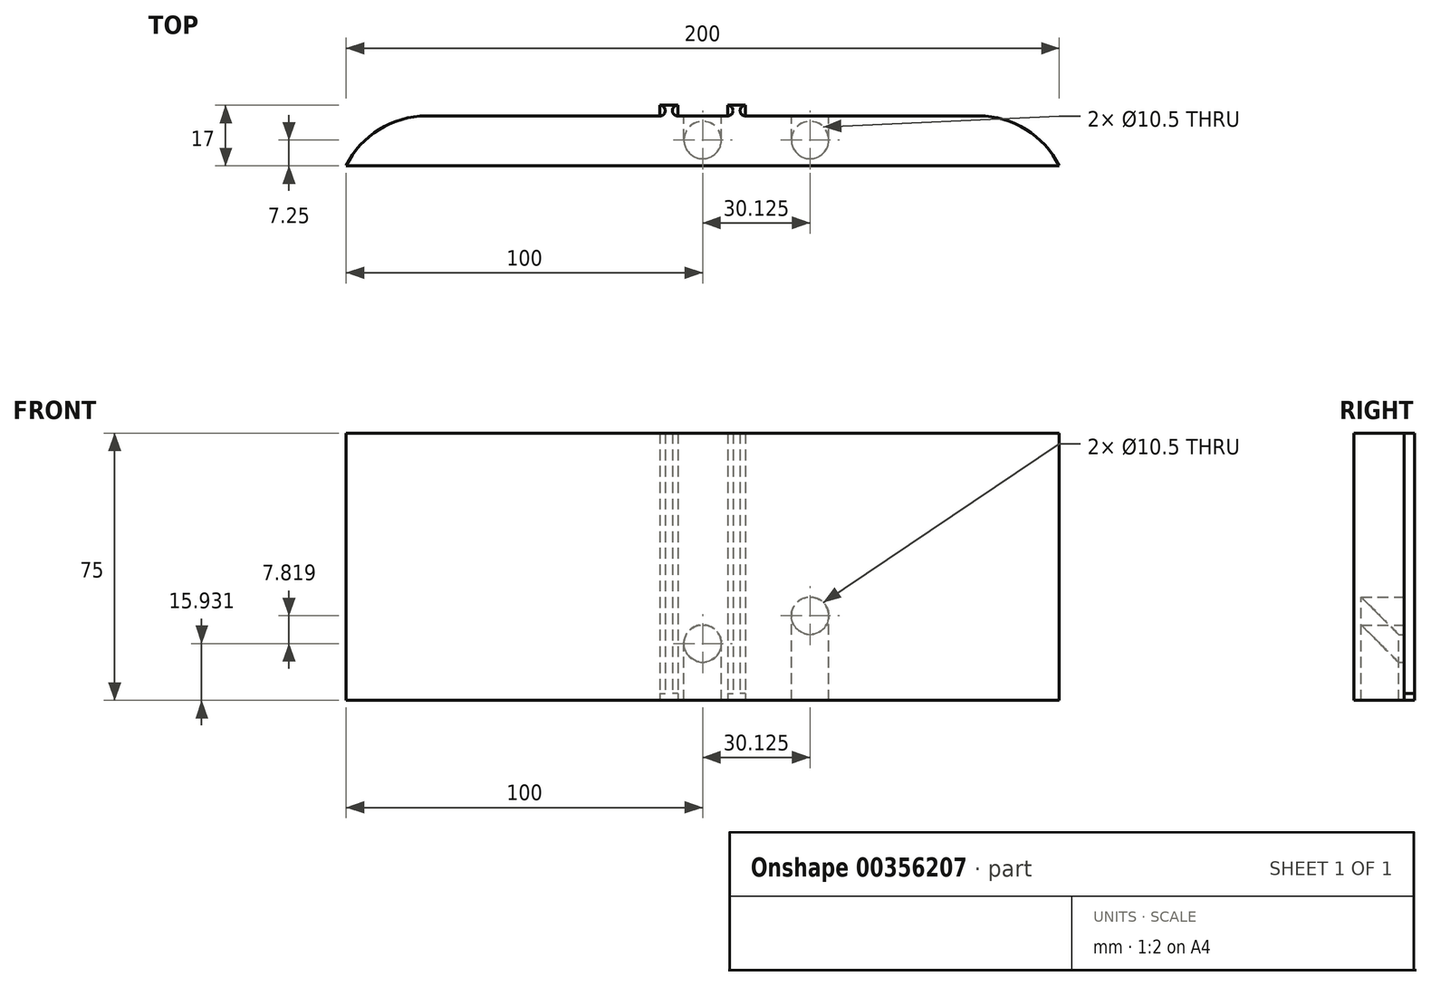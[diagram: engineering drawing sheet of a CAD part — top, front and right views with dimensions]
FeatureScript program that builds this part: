
annotation { "Feature Type Name" : "Feature", "Feature Type Description" : "" }
export const myFeature = defineFeature(function(context is Context, id is Id, definition is map)
    precondition{}
    {
        {
            var Q0;
            Q0=qCreatedBy(makeId("Top.planeOp"),FACE);
            var sketch = newSketch(context, id + "F0", { "sketchPlane" : qUnion([Q0])});
            skLineSegment(sketch, "E0.bottom", {"start": v(-13.85, 0) * mm, "end": v(12.1, 0) * mm});
            skLineSegment(sketch, "E0.top", {"start": v(-77.5, 14) * mm, "end": v(-12, 14) * mm});
            skArc(sketch, "E1", {"start": v(100, 0) * mm, "mid": v(90.75, 10.21) * mm, "end": v(77.5, 14) * mm});
            skArc(sketch, "E2", {"start": v(-77.5, 14) * mm, "mid": v(-90.75, 10.21) * mm, "end": v(-100, 0) * mm});
            skLineSegment(sketch, "E3", {"start": v(-100, 0) * mm, "end": v(-13.85, 0) * mm});
            skLineSegment(sketch, "E4", {"start": v(12.1, 0) * mm, "end": v(100, 0) * mm});
            skLineSegment(sketch, "E5.top", {"start": v(-12, 17) * mm, "end": v(-7, 17) * mm});
            skLineSegment(sketch, "E6.top", {"start": v(7, 17) * mm, "end": v(12, 17) * mm});
            skLineSegment(sketch, "E7.trimOffspring", {"start": v(-7, 14) * mm, "end": v(7, 14) * mm});
            skLineSegment(sketch, "E8.trimOffspring", {"start": v(12, 14) * mm, "end": v(77.5, 14) * mm});
            skCircle(sketch, "E9", {"center": v(30.13, 7.25) * mm, "radius": 5.25 * mm});
            skLineSegment(sketch, "E10.bottom", {"start": v(27, 14) * mm, "end": v(32.6, 14) * mm});
            skLineSegment(sketch, "E10.top", {"start": v(26.88, 11.37) * mm, "end": v(26.88, 11.37) * mm});
            skArc(sketch, "E11", {"start": v(-7, 17) * mm, "mid": v(-8.5, 15.5) * mm, "end": v(-7, 14) * mm});
            skArc(sketch, "E12", {"start": v(7, 14) * mm, "mid": v(8.5, 15.5) * mm, "end": v(7, 17) * mm});
            skArc(sketch, "E13", {"start": v(12, 17) * mm, "mid": v(10.5, 15.5) * mm, "end": v(12, 14) * mm});
            skPoint(sketch, "E14.start.orphan", {"position": v(-10.87, 14) * mm});
            skArc(sketch, "E15", {"start": v(-12, 14) * mm, "mid": v(-10.5, 15.5) * mm, "end": v(-12, 17) * mm});
            skPoint(sketch, "E10.right.end.orphan", {"position": v(33.38, 11.37) * mm});
            skLineSegment(sketch, "E16", {"start": v(7, 14) * mm, "end": v(7, 17) * mm});
            skLineSegment(sketch, "E17", {"start": v(12, 17) * mm, "end": v(12, 14) * mm});
            skLineSegment(sketch, "E18", {"start": v(-12, 14) * mm, "end": v(-12, 17) * mm});
            skLineSegment(sketch, "E19", {"start": v(-7, 17) * mm, "end": v(-7, 14) * mm});
            skLineSegment(sketch, "E20", {"start": v(-7, 14) * mm, "end": v(-12, 14) * mm});
            skLineSegment(sketch, "E21", {"start": v(12, 14) * mm, "end": v(7, 14) * mm});
            skCircle(sketch, "E22", {"center": v(0, 7.25) * mm, "radius": 5.25 * mm});
            skSolve(sketch);
        }
        {
            var Q0;
            Q0=makeQuery(id+"F0.imprint","IMPRINT",FACE,{"disambiguationData":[TD([[makeQuery(id+"F0.imprint","IMPRINT",EDGE,{"derivedFrom":sQuery(id+"F0.wireOp",EDGE,"E0.bottom")}),1.0]])]});
            var Q1;
            {var subQ0=sQuery(id+"F0.wireOp",EDGE,"E9");var subQ1=makeQuery(id+"F0.imprint","INTERSECT",VERTEX,{"derivedFrom":[subQ0,sQuery(id+"F0.wireOp",EDGE,"E10.left")]});Q1=makeQuery(id+"F0.imprint","IMPRINT",FACE,{"disambiguationData":[TD([[makeQuery(id+"F0.imprint","IMPRINT",EDGE,{"disambiguationData":[TD([[subQ1,1.0]])],"derivedFrom":subQ0}),1.0]])]});}
            var Q2;
            Q2=makeQuery(id+"F0.imprint","IMPRINT",FACE,{"disambiguationData":[TD([[makeQuery(id+"F0.imprint","IMPRINT",EDGE,{"derivedFrom":sQuery(id+"F0.wireOp",EDGE,"E10.bottom")}),-1.0]])]});
            var Q3;
            Q3=makeQuery(id+"F0.imprint","IMPRINT",FACE,{"disambiguationData":[TD([[makeQuery(id+"F0.imprint","IMPRINT",EDGE,{"derivedFrom":sQuery(id+"F0.wireOp",EDGE,"E9")}),1.0]])]});
            var Q4;
            Q4=makeQuery(id+"F0.imprint","IMPRINT",FACE,{"disambiguationData":[TD([[makeQuery(id+"F0.imprint","IMPRINT",EDGE,{"derivedFrom":sQuery(id+"F0.wireOp",EDGE,"E5.top")}),-1.0]])]});
            var Q5;
            Q5=makeQuery(id+"F0.imprint","IMPRINT",FACE,{"disambiguationData":[TD([[makeQuery(id+"F0.imprint","IMPRINT",EDGE,{"derivedFrom":sQuery(id+"F0.wireOp",EDGE,"E6.top")}),-1.0]])]});
            var Q6;
            Q6=makeQuery(id+"F0.imprint","IMPRINT",FACE,{"disambiguationData":[TD([[makeQuery(id+"F0.imprint","IMPRINT",EDGE,{"derivedFrom":sQuery(id+"F0.wireOp",EDGE,"E22")}),1.0]])]});
            extrude(context, id + "F1", {"entities" : qUnion([Q0, Q1, Q2, Q3, Q4, Q5, Q6]), "depth" : 75 * mm});
        }
        {
            var Q0;
            Q0=sQuery(id+"F0.wireOp",VERTEX,"E9.center");
            var Q1;
            Q1=qCreatedBy(makeId("Right.planeOp"),FACE);
            cPlane(context, id + "F2", {"entities" : qUnion([Q0, Q1]), "cplaneType" : CPlaneType.PLANE_POINT, "offset" : 25 * mm, "width" : 150 * mm, "height" : 150 * mm});
        }
        {
            var Q0;
            Q0=qCreatedBy(id+"F2.planeOp",FACE);
            var sketch = newSketch(context, id + "F3", { "sketchPlane" : qUnion([Q0])});
            skLineSegment(sketch, "E23", {"start": v(8, 0) * mm, "end": v(8, 23) * mm});
            skLineSegment(sketch, "E24", {"start": v(8, 23) * mm, "end": v(14, 23) * mm});
            skSolve(sketch);
        }
        {
            var Q0;
            Q0=makeQuery(id+"F0.imprint","IMPRINT",FACE,{"disambiguationData":[TD([[makeQuery(id+"F0.imprint","IMPRINT",EDGE,{"derivedFrom":sQuery(id+"F0.wireOp",EDGE,"E13")}),1.0]])]});
            var Q1;
            Q1=makeQuery(id+"F0.imprint","IMPRINT",FACE,{"disambiguationData":[TD([[makeQuery(id+"F0.imprint","IMPRINT",EDGE,{"derivedFrom":sQuery(id+"F0.wireOp",EDGE,"E12")}),1.0]])]});
            var Q2;
            Q2=makeQuery(id+"F0.imprint","IMPRINT",FACE,{"disambiguationData":[TD([[makeQuery(id+"F0.imprint","IMPRINT",EDGE,{"derivedFrom":sQuery(id+"F0.wireOp",EDGE,"E11")}),1.0]])]});
            var Q3;
            Q3=makeQuery(id+"F0.imprint","IMPRINT",FACE,{"disambiguationData":[TD([[makeQuery(id+"F0.imprint","IMPRINT",EDGE,{"derivedFrom":sQuery(id+"F0.wireOp",EDGE,"E15")}),1.0]])]});
            var Q4;
            Q4=makeQuery(id+"F0.imprint","IMPRINT",FACE,{"disambiguationData":[TD([[makeQuery(id+"F0.imprint","IMPRINT",EDGE,{"derivedFrom":sQuery(id+"F0.wireOp",EDGE,"E5.top")}),-1.0]])]});
            var Q5;
            Q5=makeQuery(id+"F0.imprint","IMPRINT",FACE,{"disambiguationData":[TD([[makeQuery(id+"F0.imprint","IMPRINT",EDGE,{"derivedFrom":sQuery(id+"F0.wireOp",EDGE,"E6.top")}),-1.0]])]});
            extrude(context, id + "F4", {"entities" : qUnion([Q0, Q1, Q2, Q3, Q4, Q5]), "operationType" : NewBodyOperationType.ADD, "depth" : 2 * mm});
        }
        {
            var Q0;
            {var subQ0=sQuery(id+"F0.wireOp",EDGE,"E9");var subQ1=makeQuery(id+"F0.imprint","INTERSECT",VERTEX,{"derivedFrom":[subQ0,sQuery(id+"F0.wireOp",EDGE,"E10.left")]});Q0=makeQuery(id+"F0.imprint","IMPRINT",FACE,{"disambiguationData":[TD([[makeQuery(id+"F0.imprint","IMPRINT",EDGE,{"disambiguationData":[TD([[subQ1,1.0]])],"derivedFrom":subQ0}),1.0]])]});}
            var Q1;
            Q1=makeQuery(id+"F0.imprint","IMPRINT",FACE,{"disambiguationData":[TD([[makeQuery(id+"F0.imprint","IMPRINT",EDGE,{"derivedFrom":sQuery(id+"F0.wireOp",EDGE,"E9")}),1.0]])]});
            var Q2;
            Q2=sQuery(id+"F3.wireOp",EDGE,"E23");
            var Q3;
            Q3=sQuery(id+"F3.wireOp",EDGE,"E24");
            sweep(context, id + "F5", {"operationType" : NewBodyOperationType.REMOVE, "profiles" : qUnion([Q0, Q1]), "path" : qUnion([Q2, Q3])});
        }
        {
            var Q0;
            Q0=qCreatedBy(makeId("Right.planeOp"),FACE);
            var sketch = newSketch(context, id + "F6", { "sketchPlane" : qUnion([Q0])});
            skLineSegment(sketch, "E25", {"start": v(9.3, 0) * mm, "end": v(9.3, 13.88) * mm});
            skLineSegment(sketch, "E26", {"start": v(23.78, 13.88) * mm, "end": v(9.3, 13.88) * mm});
            skSolve(sketch);
        }
        {
            var Q0;
            Q0=makeQuery(id+"F0.imprint","IMPRINT",FACE,{"disambiguationData":[TD([[makeQuery(id+"F0.imprint","IMPRINT",EDGE,{"derivedFrom":sQuery(id+"F0.wireOp",EDGE,"E22")}),1.0]])]});
            var Q1;
            Q1=sQuery(id+"F6.wireOp",EDGE,"E26");
            var Q2;
            Q2=sQuery(id+"F6.wireOp",EDGE,"E25");
            sweep(context, id + "F7", {"operationType" : NewBodyOperationType.REMOVE, "profiles" : qUnion([Q0]), "path" : qUnion([Q1, Q2])});
        }
    });
